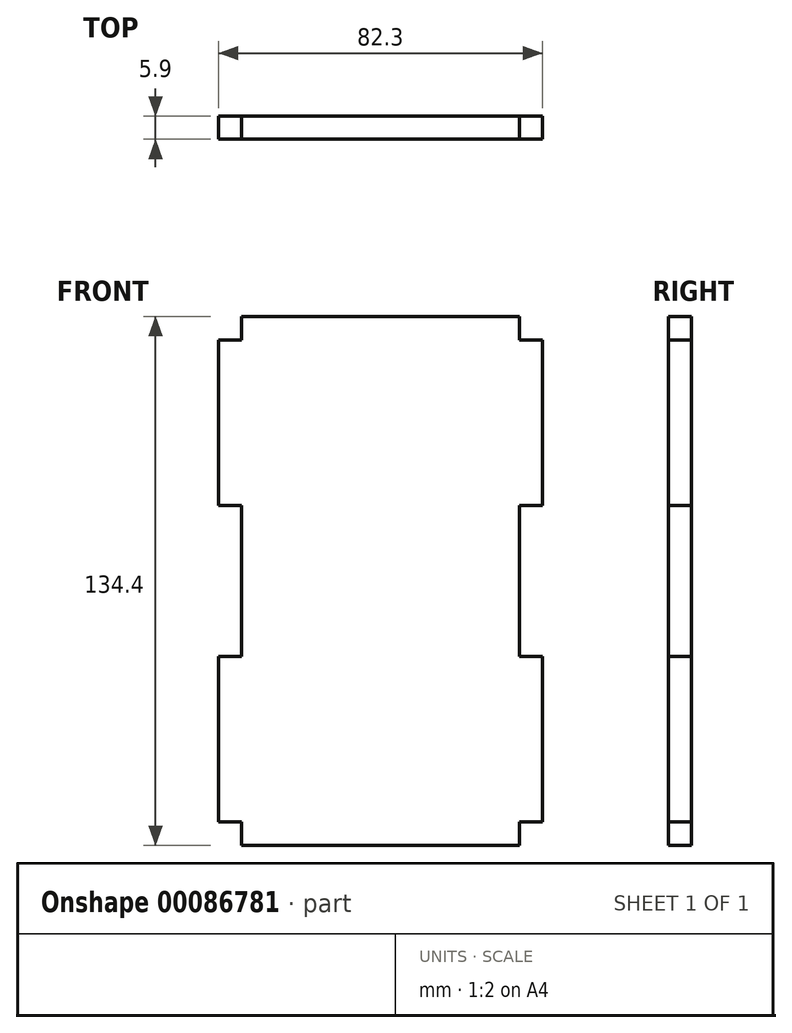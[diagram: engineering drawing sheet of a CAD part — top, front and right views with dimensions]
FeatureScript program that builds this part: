
annotation { "Feature Type Name" : "Feature", "Feature Type Description" : "" }
export const myFeature = defineFeature(function(context is Context, id is Id, definition is map)
    precondition{}
    {
        {
            var Q0;
            Q0=qCreatedBy(makeId("Front.planeOp"),FACE);
            var sketch = newSketch(context, id + "F0", { "sketchPlane" : qUnion([Q0])});
            skLineSegment(sketch, "E0.bottom", {"start": v(35.25, 67.2) * mm, "end": v(-35.25, 67.2) * mm});
            skLineSegment(sketch, "E0.top", {"start": v(35.25, -67.2) * mm, "end": v(-35.25, -67.2) * mm});
            skLineSegment(sketch, "E0.left", {"start": v(35.25, 67.2) * mm, "end": v(35.25, -67.2) * mm});
            skLineSegment(sketch, "E0.right", {"start": v(-35.25, 67.2) * mm, "end": v(-35.25, -67.2) * mm});
            skPoint(sketch, "E0.middle", {"position": v(0, 0) * mm});
            skLineSegment(sketch, "E1.bottom", {"start": v(-35.25, 61.2) * mm, "end": v(-41.15, 61.2) * mm});
            skLineSegment(sketch, "E1.top", {"start": v(-35.25, 19.2) * mm, "end": v(-41.15, 19.2) * mm});
            skLineSegment(sketch, "E1.left", {"start": v(-35.25, 61.2) * mm, "end": v(-35.25, 19.2) * mm});
            skLineSegment(sketch, "E1.right", {"start": v(-41.15, 61.2) * mm, "end": v(-41.15, 19.2) * mm});
            skLineSegment(sketch, "E2.MirrorCS", {"start": v(35.25, 61.2) * mm, "end": v(41.15, 61.2) * mm});
            skLineSegment(sketch, "E3.MirrorCS", {"start": v(41.15, 61.2) * mm, "end": v(41.15, 19.2) * mm});
            skLineSegment(sketch, "E4.MirrorCS", {"start": v(35.25, 19.2) * mm, "end": v(41.15, 19.2) * mm});
            skLineSegment(sketch, "E5.MirrorCS", {"start": v(-35.25, -19.2) * mm, "end": v(-41.15, -19.2) * mm});
            skLineSegment(sketch, "E6.MirrorCS", {"start": v(-41.15, -61.2) * mm, "end": v(-41.15, -19.2) * mm});
            skLineSegment(sketch, "E7.MirrorCS", {"start": v(-35.25, -61.2) * mm, "end": v(-41.15, -61.2) * mm});
            skLineSegment(sketch, "E8.MirrorCS", {"start": v(35.25, -61.2) * mm, "end": v(41.15, -61.2) * mm});
            skLineSegment(sketch, "E9.MirrorCS", {"start": v(41.15, -61.2) * mm, "end": v(41.15, -19.2) * mm});
            skLineSegment(sketch, "E10.MirrorCS", {"start": v(35.25, -19.2) * mm, "end": v(41.15, -19.2) * mm});
            skSolve(sketch);
        }
        {
            var Q0;
            Q0 = qSketchRegion(id + "F0", true);
            extrude(context, id + "F1", {"entities" : qUnion([Q0]), "depth" : 5.9 * mm});
        }
    });
